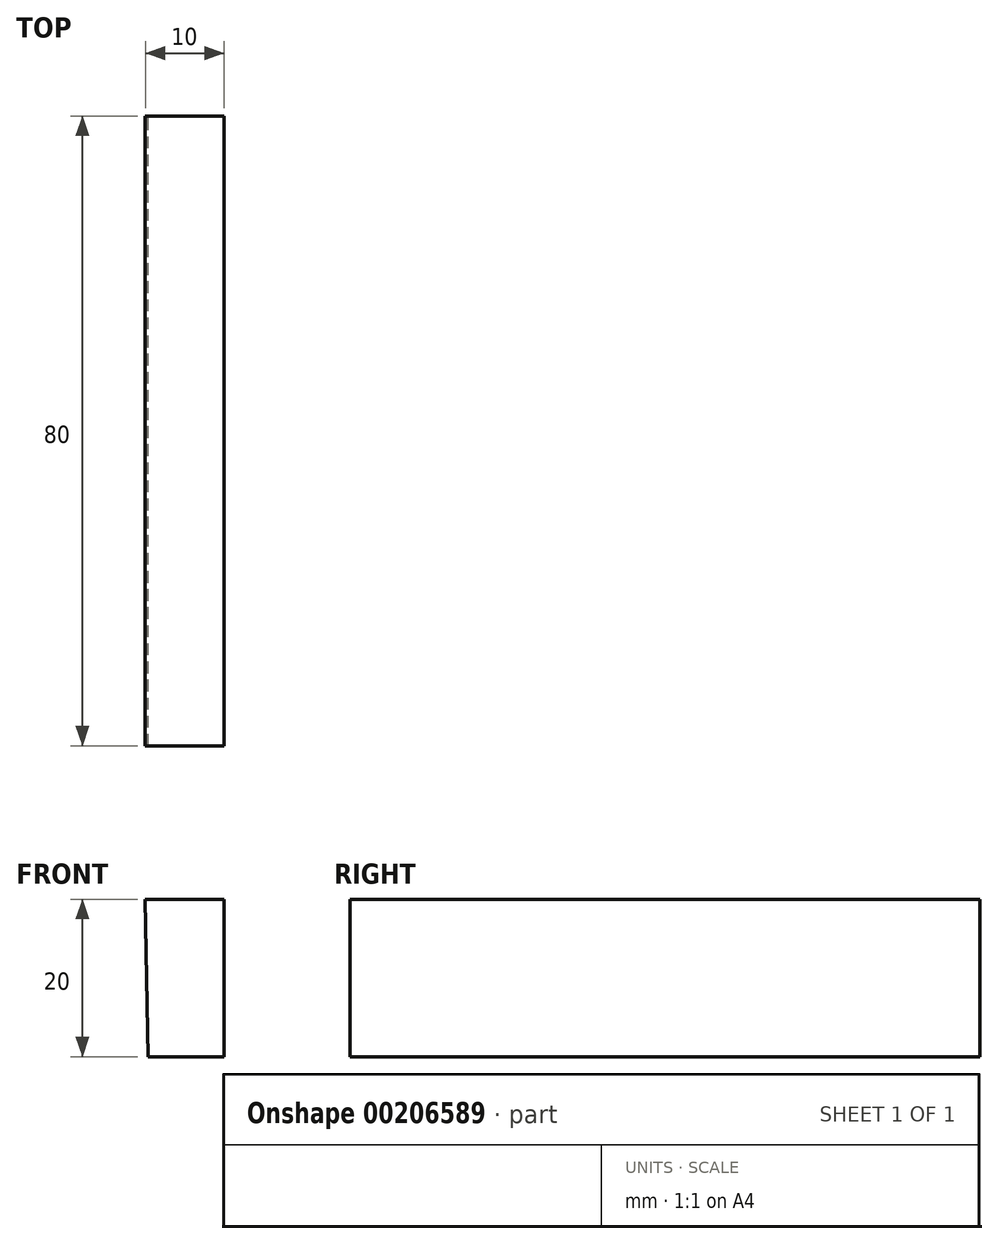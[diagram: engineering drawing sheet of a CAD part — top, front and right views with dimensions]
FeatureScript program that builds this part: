
annotation { "Feature Type Name" : "Feature", "Feature Type Description" : "" }
export const myFeature = defineFeature(function(context is Context, id is Id, definition is map)
    precondition{}
    {
        {
            var Q0;
            Q0=qCreatedBy(makeId("Front.planeOp"),FACE);
            var sketch = newSketch(context, id + "F0", { "sketchPlane" : qUnion([Q0])});
            skLineSegment(sketch, "E0", {"start": v(-60.2, 36.18) * mm, "end": v(-59.85, 16.18) * mm});
            skLineSegment(sketch, "E1", {"start": v(-59.85, 16.18) * mm, "end": v(-50.2, 16.18) * mm});
            skLineSegment(sketch, "E2", {"start": v(-50.2, 16.18) * mm, "end": v(-50.2, 36.18) * mm});
            skLineSegment(sketch, "E3", {"start": v(-50.2, 36.18) * mm, "end": v(-60.2, 36.18) * mm});
            skSolve(sketch);
        }
        {
            var Q0;
            Q0=makeQuery(id+"F0.imprint","IMPRINT",FACE,{"disambiguationData":[TD([[makeQuery(id+"F0.imprint","IMPRINT",EDGE,{"derivedFrom":sQuery(id+"F0.wireOp",EDGE,"E0")}),1.0]])]});
            extrude(context, id + "F1", {"entities" : qUnion([Q0]), "depth" : 80 * mm});
        }
    });
